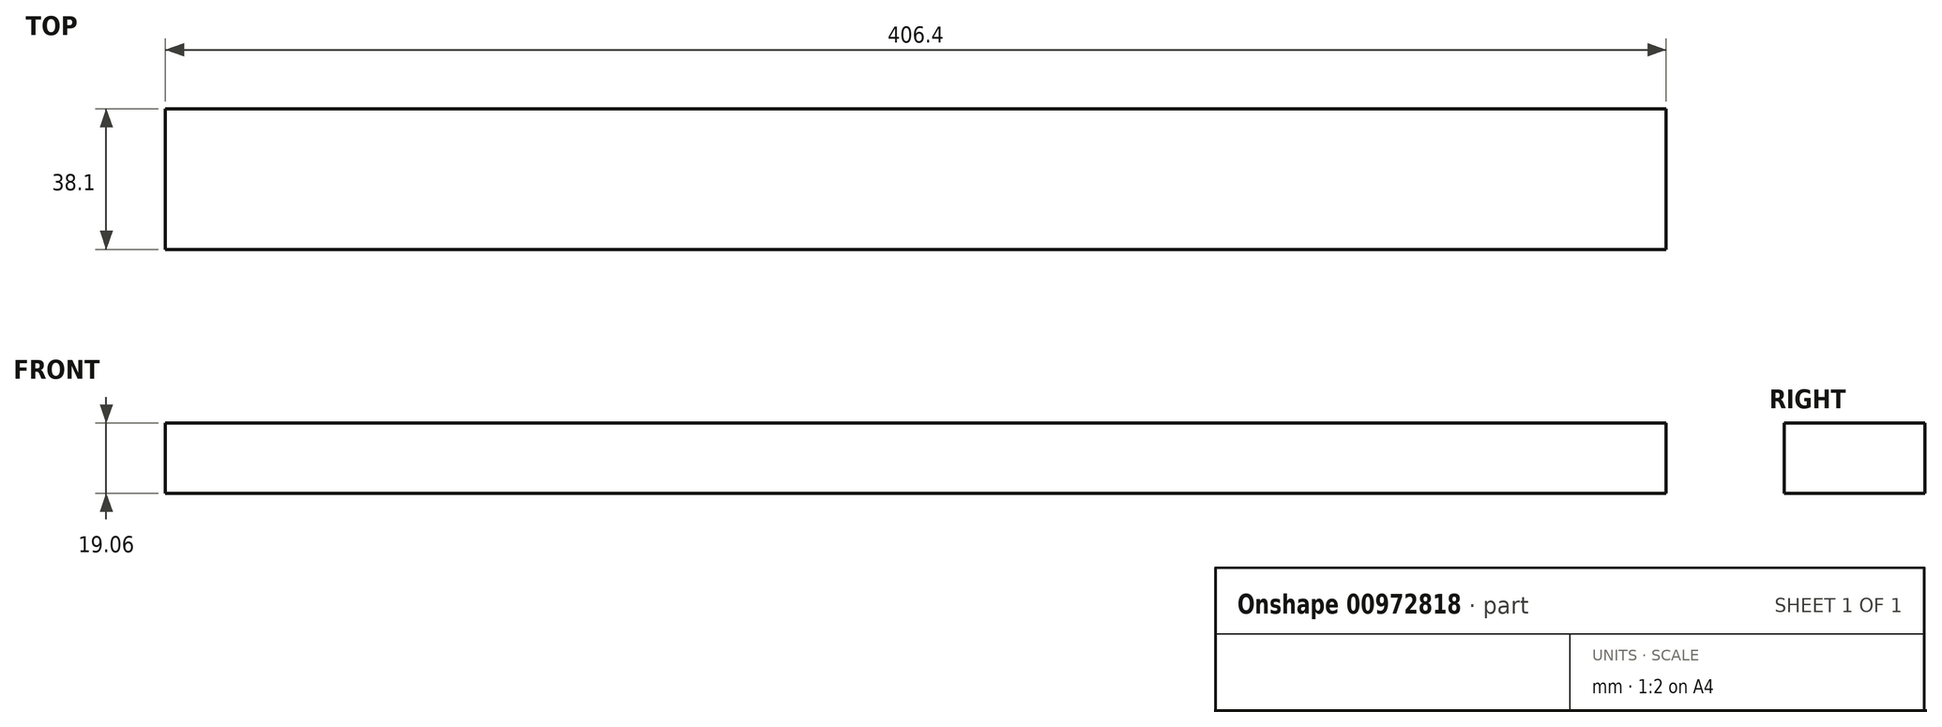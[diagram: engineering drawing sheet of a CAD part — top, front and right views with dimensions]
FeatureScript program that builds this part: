
annotation { "Feature Type Name" : "Feature", "Feature Type Description" : "" }
export const myFeature = defineFeature(function(context is Context, id is Id, definition is map)
    precondition{}
    {
        {
            var Q0;
            Q0=qCreatedBy(makeId("Right.planeOp"),FACE);
            var sketch = newSketch(context, id + "F0", { "sketchPlane" : qUnion([Q0])});
            skLineSegment(sketch, "E0.bottom", {"start": v(19.05, 9.53) * mm, "end": v(-19.05, 9.53) * mm});
            skLineSegment(sketch, "E0.top", {"start": v(19.05, -9.53) * mm, "end": v(-19.05, -9.53) * mm});
            skLineSegment(sketch, "E0.left", {"start": v(19.05, 9.53) * mm, "end": v(19.05, -9.53) * mm});
            skLineSegment(sketch, "E0.right", {"start": v(-19.05, 9.53) * mm, "end": v(-19.05, -9.53) * mm});
            skPoint(sketch, "E0.middle", {"position": v(0, 0) * mm});
            skSolve(sketch);
        }
        {
            var Q0;
            Q0=makeQuery(id+"F0.imprint","IMPRINT",FACE,{"disambiguationData":[TD([[makeQuery(id+"F0.imprint","IMPRINT",EDGE,{"derivedFrom":sQuery(id+"F0.wireOp",EDGE,"E0.bottom")}),1.0]])]});
            extrude(context, id + "F1", {"entities" : qUnion([Q0]), "depth" : 406.4 * mm, "offsetDistance" : 25.4 * mm});
        }
    });
